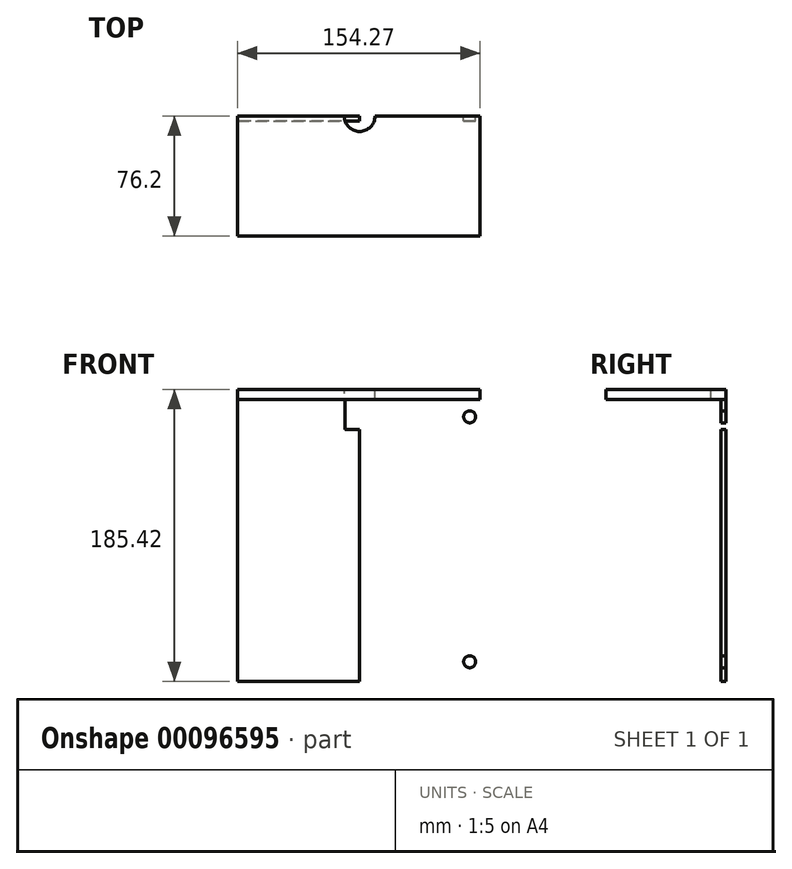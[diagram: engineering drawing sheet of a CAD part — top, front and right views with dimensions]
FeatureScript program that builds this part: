
annotation { "Feature Type Name" : "Feature", "Feature Type Description" : "" }
export const myFeature = defineFeature(function(context is Context, id is Id, definition is map)
    precondition{}
    {
        {
            var Q0;
            Q0=qCreatedBy(makeId("Front.planeOp"),FACE);
            var sketch = newSketch(context, id + "F0", { "sketchPlane" : qUnion([Q0])});
            skLineSegment(sketch, "E0.bottom", {"start": v(-69.85, 77.79) * mm, "end": v(69.85, 77.79) * mm});
            skLineSegment(sketch, "E0.top", {"start": v(-69.85, -77.79) * mm, "end": v(69.85, -77.79) * mm});
            skLineSegment(sketch, "E0.left", {"start": v(-69.85, 77.79) * mm, "end": v(-69.85, -77.79) * mm});
            skLineSegment(sketch, "E0.right", {"start": v(69.85, 77.79) * mm, "end": v(69.85, -77.79) * mm});
            skPoint(sketch, "E0.middle", {"position": v(0, 0) * mm});
            skCircle(sketch, "E1", {"center": v(-69.85, -77.79) * mm, "radius": 3.81 * mm});
            skCircle(sketch, "E2", {"center": v(69.85, -77.79) * mm, "radius": 3.81 * mm});
            skCircle(sketch, "E3", {"center": v(69.85, 77.79) * mm, "radius": 3.81 * mm});
            skCircle(sketch, "E4", {"center": v(-69.85, 77.79) * mm, "radius": 3.81 * mm});
            skLineSegment(sketch, "E5", {"start": v(0, -77.79) * mm, "end": v(0, -90.31) * mm});
            skLineSegment(sketch, "E6", {"start": v(0, -90.31) * mm, "end": v(0, -77.79) * mm});
            skLineSegment(sketch, "E7", {"start": v(0, -90.31) * mm, "end": v(0, 88.74) * mm});
            skPoint(sketch, "E7.endSnap0", {"position": v(0, 77.79) * mm});
            skLineSegment(sketch, "E8", {"start": v(0, 88.74) * mm, "end": v(0, -90.31) * mm});
            skLineSegment(sketch, "E9", {"start": v(0, 0) * mm, "end": v(76.56, 0) * mm});
            skLineSegment(sketch, "E10", {"start": v(76.56, 0) * mm, "end": v(-77.71, 0) * mm});
            skLineSegment(sketch, "E11", {"start": v(-77.71, 0) * mm, "end": v(76.56, 0) * mm});
            skLineSegment(sketch, "E12", {"start": v(-77.71, 0) * mm, "end": v(-77.71, 88.74) * mm});
            skLineSegment(sketch, "E13", {"start": v(-77.71, 88.74) * mm, "end": v(76.56, 88.74) * mm});
            skLineSegment(sketch, "E14", {"start": v(76.56, 88.74) * mm, "end": v(76.56, -90.31) * mm});
            skLineSegment(sketch, "E15", {"start": v(76.56, -90.31) * mm, "end": v(-77.71, -90.31) * mm});
            skLineSegment(sketch, "E16", {"start": v(-77.71, -90.31) * mm, "end": v(-77.71, 0) * mm});
            skSolve(sketch);
        }
        {
            var Q0;
            {var subQ10=sQuery(id+"F0.wireOp",EDGE,"E12");Q0=makeQuery(id+"F0.imprint","IMPRINT",FACE,{"disambiguationData":[TD([[makeQuery(id+"F0.imprint","IMPRINT",EDGE,{"derivedFrom":subQ10}),-1.0]])]});}
            var Q1;
            {var subQ1=sQuery(id+"F0.wireOp",EDGE,"E8");var subQ3=sQuery(id+"F0.wireOp",EDGE,"E0.bottom");var subQ4=makeQuery(id+"F0.imprint","INTERSECT",VERTEX,{"derivedFrom":[subQ3,subQ1]});Q1=makeQuery(id+"F0.imprint","IMPRINT",FACE,{"disambiguationData":[TD([[makeQuery(id+"F0.imprint","IMPRINT",EDGE,{"disambiguationData":[TD([[subQ4,-1.0]])],"derivedFrom":subQ3}),1.0]])]});}
            var Q2;
            {var subQ1=sQuery(id+"F0.wireOp",EDGE,"E8");var subQ3=sQuery(id+"F0.wireOp",EDGE,"E0.top");var subQ4=makeQuery(id+"F0.imprint","INTERSECT",VERTEX,{"derivedFrom":[subQ3,subQ1]});Q2=makeQuery(id+"F0.imprint","IMPRINT",FACE,{"disambiguationData":[TD([[makeQuery(id+"F0.imprint","IMPRINT",EDGE,{"disambiguationData":[TD([[subQ4,-1.0]])],"derivedFrom":subQ3}),-1.0]])]});}
            var Q3;
            {var subQ9=sQuery(id+"F0.wireOp",EDGE,"E16");Q3=makeQuery(id+"F0.imprint","IMPRINT",FACE,{"disambiguationData":[TD([[makeQuery(id+"F0.imprint","IMPRINT",EDGE,{"derivedFrom":subQ9}),-1.0]])]});}
            var Q4;
            {var subQ0=sQuery(id+"F0.wireOp",EDGE,"E1");var subQ1=sQuery(id+"F0.wireOp",EDGE,"E0.top");var subQ2=makeQuery(id+"F0.imprint","INTERSECT",VERTEX,{"derivedFrom":[subQ1,subQ0]});Q4=makeQuery(id+"F0.imprint","IMPRINT",FACE,{"disambiguationData":[TD([[makeQuery(id+"F0.imprint","IMPRINT",EDGE,{"disambiguationData":[TD([[subQ2,-1.0]])],"derivedFrom":subQ1}),1.0]])]});}
            var Q5;
            {var subQ1=sQuery(id+"F0.wireOp",EDGE,"E0.bottom");var subQ5=sQuery(id+"F0.wireOp",EDGE,"E4");var subQ9=makeQuery(id+"F0.imprint","INTERSECT",VERTEX,{"derivedFrom":[subQ1,subQ5]});Q5=makeQuery(id+"F0.imprint","IMPRINT",FACE,{"disambiguationData":[TD([[makeQuery(id+"F0.imprint","IMPRINT",EDGE,{"disambiguationData":[TD([[subQ9,-1.0]])],"derivedFrom":subQ1}),-1.0]])]});}
            var Q6;
            {var subQ0=sQuery(id+"F0.wireOp",EDGE,"E8");var subQ1=sQuery(id+"F0.wireOp",EDGE,"E0.bottom");var subQ2=makeQuery(id+"F0.imprint","INTERSECT",VERTEX,{"derivedFrom":[subQ1,subQ0]});Q6=makeQuery(id+"F0.imprint","IMPRINT",FACE,{"disambiguationData":[TD([[makeQuery(id+"F0.imprint","IMPRINT",EDGE,{"disambiguationData":[TD([[subQ2,-1.0]])],"derivedFrom":subQ1}),-1.0]])]});}
            var Q7;
            {var subQ0=sQuery(id+"F0.wireOp",EDGE,"E8");var subQ1=sQuery(id+"F0.wireOp",EDGE,"E0.top");var subQ2=makeQuery(id+"F0.imprint","INTERSECT",VERTEX,{"derivedFrom":[subQ1,subQ0]});Q7=makeQuery(id+"F0.imprint","IMPRINT",FACE,{"disambiguationData":[TD([[makeQuery(id+"F0.imprint","IMPRINT",EDGE,{"disambiguationData":[TD([[subQ2,-1.0]])],"derivedFrom":subQ1}),1.0]])]});}
            extrude(context, id + "F1", {"entities" : qUnion([Q0, Q1, Q2, Q3, Q4, Q5, Q6, Q7]), "depth" : 3.17 * mm});
        }
        {
            var Q0;
            Q0=makeQuery(id+"F1.opExtrude","CAP_FACE",FACE,{"disambiguationData":[OSD([sQuery(id+"F0.wireOp",EDGE,"E1"),sQuery(id+"F0.wireOp",EDGE,"E2"),sQuery(id+"F0.wireOp",EDGE,"E3"),sQuery(id+"F0.wireOp",EDGE,"E4"),sQuery(id+"F0.wireOp",EDGE,"E12"),sQuery(id+"F0.wireOp",EDGE,"E13"),sQuery(id+"F0.wireOp",EDGE,"E14"),sQuery(id+"F0.wireOp",EDGE,"E15"),sQuery(id+"F0.wireOp",EDGE,"E16")])],"isStart":true});
            var sketch = newSketch(context, id + "F2", { "sketchPlane" : qUnion([Q0])});
            skLineSegment(sketch, "E17.bottom", {"start": v(-76.56, 88.74) * mm, "end": v(77.71, 88.74) * mm});
            skLineSegment(sketch, "E17.top", {"start": v(-76.56, 95.1) * mm, "end": v(77.71, 95.1) * mm});
            skLineSegment(sketch, "E17.left", {"start": v(-76.56, 88.74) * mm, "end": v(-76.56, 95.1) * mm});
            skLineSegment(sketch, "E17.right", {"start": v(77.71, 88.74) * mm, "end": v(77.71, 95.1) * mm});
            skSolve(sketch);
        }
        {
            var Q0;
            Q0 = qSketchRegion(id + "F2", true);
            extrude(context, id + "F3", {"entities" : qUnion([Q0]), "operationType" : NewBodyOperationType.ADD, "oppositeDirection" : true, "depth" : 76.2 * mm});
        }
        {
            var Q0;
            Q0=makeQuery(id+"F3.opExtrude","SWEPT_FACE",FACE,{"disambiguationData":[OSD([sQuery(id+"F2.wireOp",EDGE,"E17.top")])]});
            var sketch = newSketch(context, id + "F4", { "sketchPlane" : qUnion([Q0])});
            skCircle(sketch, "E18", {"center": v(0, 0) * mm, "radius": 9.75 * mm});
            skSolve(sketch);
        }
        {
            var Q0;
            Q0 = qSketchRegion(id + "F4", true);
            extrude(context, id + "F5", {"entities" : qUnion([Q0]), "operationType" : NewBodyOperationType.REMOVE, "oppositeDirection" : true, "depth" : 25.4 * mm});
        }
    });
